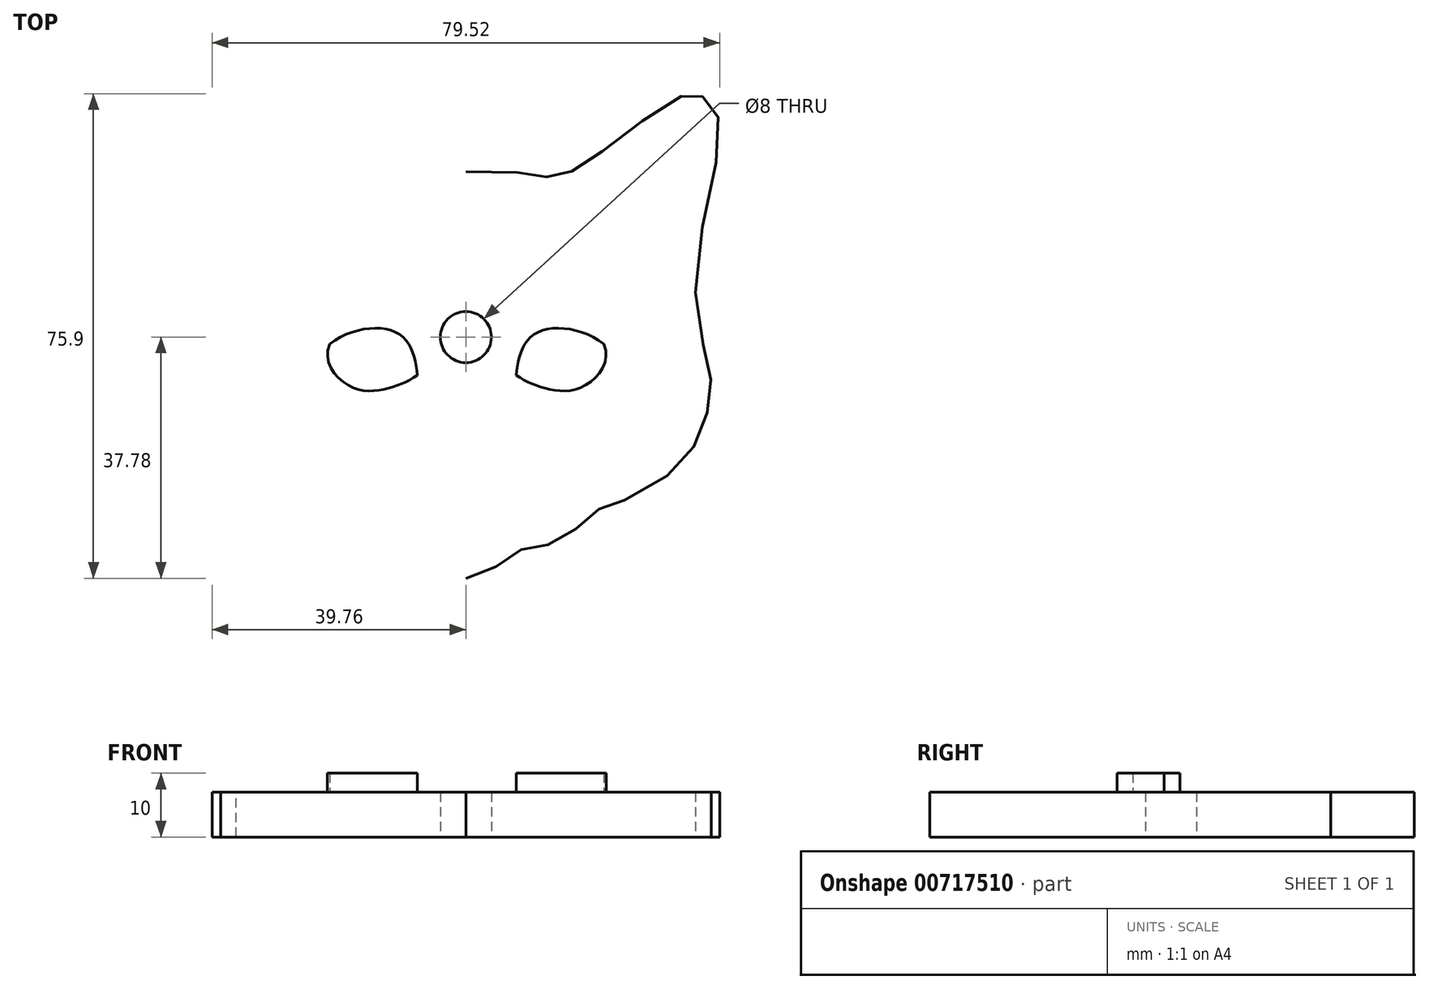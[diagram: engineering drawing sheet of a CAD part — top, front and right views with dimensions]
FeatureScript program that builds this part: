
annotation { "Feature Type Name" : "Feature", "Feature Type Description" : "" }
export const myFeature = defineFeature(function(context is Context, id is Id, definition is map)
    precondition{}
    {
        {
            assignVariable(context, id + "F0", {"name" : "thickness", "anyValue" : 7 * mm});
        }
        {
            var Q0;
            Q0=qCreatedBy(makeId("Top.planeOp"),FACE);
            var sketch = newSketch(context, id + "F1", { "sketchPlane" : qUnion([Q0])});
            skCircle(sketch, "E0", {"center": v(0, 0) * mm, "radius": 11 * mm});
            skCircle(sketch, "E1", {"center": v(0, 0) * mm, "radius": 4 * mm});
            skSolve(sketch);
        }
        {
            var Q0;
            Q0=makeQuery(id+"F1.imprint","IMPRINT",FACE,{"disambiguationData":[TD([[makeQuery(id+"F1.imprint","IMPRINT",EDGE,{"derivedFrom":sQuery(id+"F1.wireOp",EDGE,"E0")}),1.0]])]});
            extrude(context, id + "F2", {"entities" : qUnion([Q0]), "depth" : getVariable(context, 'thickness'), "offsetDistance" : 25.4 * mm});
        }
        {
            var Q0;
            Q0=qCreatedBy(makeId("Top.planeOp"),FACE);
            var sketch = newSketch(context, id + "F3", { "sketchPlane" : qUnion([Q0])});
            skCircle(sketch, "E2", {"center": v(0, 0) * mm, "radius": 76.2 * mm, "construction": true});
            skCircle(sketch, "E3", {"center": v(0, 0) * mm, "radius": 11 * mm});
            skLineSegment(sketch, "E4.bottom", {"start": v(50.8, -50.8) * mm, "end": v(-50.8, -50.8) * mm, "construction": true});
            skLineSegment(sketch, "E4.top", {"start": v(50.8, 50.8) * mm, "end": v(-50.8, 50.8) * mm, "construction": true});
            skLineSegment(sketch, "E4.left", {"start": v(50.8, -50.8) * mm, "end": v(50.8, 50.8) * mm, "construction": true});
            skLineSegment(sketch, "E4.right", {"start": v(-50.8, -50.8) * mm, "end": v(-50.8, 50.8) * mm, "construction": true});
            skFitSpline(sketch, "E5", {"points": [v(0, 25.89) * mm, v(-10.97, 25.46) * mm, v(-13.35, 25.03) * mm, v(-17.23, 26.32) * mm, v(-23.92, 31.07) * mm, v(-33.85, 37.76) * mm, v(-36.23, 37.98) * mm, v(-38.6, 36.47) * mm, v(-39.68, 30.64) * mm, v(-36.01, 9.92) * mm, v(-37.74, -3.46) * mm, v(-38.38, -8.64) * mm, v(-36.66, -15.12) * mm, v(-32.77, -20.73) * mm, v(-23.28, -26.13) * mm, v(-20.69, -26.99) * mm, v(-17.02, -30.23) * mm, v(-12.48, -32.6) * mm, v(-8.82, -33.25) * mm, v(-4.93, -35.84) * mm, v(0, -37.78) * mm], "startDerivative": vector(-200.3, -0.89) * mm, "endDerivative": vector(113.08, -33.73) * mm});
            skLineSegment(sketch, "E6", {"start": v(0, 50.8) * mm, "end": v(0, -50.8) * mm, "construction": true});
            skFitSpline(sketch, "E7.MirrorCS", {"points": [v(0, 25.89) * mm, v(10.97, 25.46) * mm, v(13.35, 25.03) * mm, v(17.23, 26.32) * mm, v(23.92, 31.07) * mm, v(33.85, 37.76) * mm, v(36.23, 37.98) * mm, v(38.6, 36.47) * mm, v(39.68, 30.64) * mm, v(36.01, 9.92) * mm, v(37.74, -3.46) * mm, v(38.38, -8.64) * mm, v(36.66, -15.12) * mm, v(32.77, -20.73) * mm, v(23.28, -26.13) * mm, v(20.69, -26.99) * mm, v(17.02, -30.23) * mm, v(12.48, -32.6) * mm, v(8.82, -33.25) * mm, v(4.93, -35.84) * mm, v(0, -37.78) * mm], "startDerivative": vector(200.3, -0.89) * mm, "endDerivative": vector(-113.08, -33.73) * mm});
            skSolve(sketch);
        }
        {
            var Q0;
            Q0=makeQuery(id+"F3.imprint","IMPRINT",FACE,{"disambiguationData":[TD([[makeQuery(id+"F3.imprint","IMPRINT",EDGE,{"derivedFrom":sQuery(id+"F3.wireOp",EDGE,"E3")}),-1.0]])]});
            var Q1;
            Q1=makeQuery(id+"F2.opExtrude","CAP_FACE",FACE,{"disambiguationData":[OSD([sQuery(id+"F1.wireOp",EDGE,"E0"),sQuery(id+"F1.wireOp",EDGE,"E1")])],"isStart":false});
            extrude(context, id + "F4", {"entities" : qUnion([Q0]), "endBound" : BoundingType.UP_TO_SURFACE, "depth" : 25.4 * mm, "endBoundEntityFace" : qUnion([Q1]), "offsetDistance" : 25.4 * mm});
        }
        {
            var Q0;
            Q0=makeQuery(id+"F4.opExtrude","CAP_FACE",FACE,{"disambiguationData":[OSD([sQuery(id+"F3.wireOp",EDGE,"E3"),sQuery(id+"F3.wireOp",EDGE,"E5"),sQuery(id+"F3.wireOp",EDGE,"E7.MirrorCS")])],"isStart":false});
            var sketch = newSketch(context, id + "F5", { "sketchPlane" : qUnion([Q0])});
            skLineSegment(sketch, "E8", {"start": v(0.15, 50.37) * mm, "end": v(0.15, -51.23) * mm, "construction": true});
            skFitSpline(sketch, "E9", {"points": [v(-21.3, -1.1) * mm, v(-10.57, 0.53) * mm, v(-7.6, -6) * mm], "startDerivative": vector(17.84, 14.1) * mm, "endDerivative": vector(1.6, -16.78) * mm});
            skFitSpline(sketch, "E10", {"points": [v(-21.3, -1.1) * mm, v(-18.12, -7.71) * mm, v(-12.1, -8.01) * mm, v(-7.6, -6) * mm], "startDerivative": vector(-10.48, -22.58) * mm, "endDerivative": vector(14.09, 9.2) * mm});
            skFitSpline(sketch, "E11.MirrorCS", {"points": [v(21.59, -1.1) * mm, v(18.4, -7.71) * mm, v(12.38, -8.01) * mm, v(7.89, -6) * mm], "startDerivative": vector(10.48, -22.58) * mm, "endDerivative": vector(-14.09, 9.2) * mm});
            skFitSpline(sketch, "E12.MirrorCS", {"points": [v(21.59, -1.1) * mm, v(10.87, 0.53) * mm, v(7.89, -6) * mm], "startDerivative": vector(-17.84, 14.1) * mm, "endDerivative": vector(-1.6, -16.78) * mm});
            skSolve(sketch);
        }
        {
            var Q0;
            Q0 = qSketchRegion(id + "F5", true);
            extrude(context, id + "F6", {"entities" : qUnion([Q0]), "operationType" : NewBodyOperationType.ADD, "depth" : 3 * mm, "offsetDistance" : 25.4 * mm});
        }
    });
